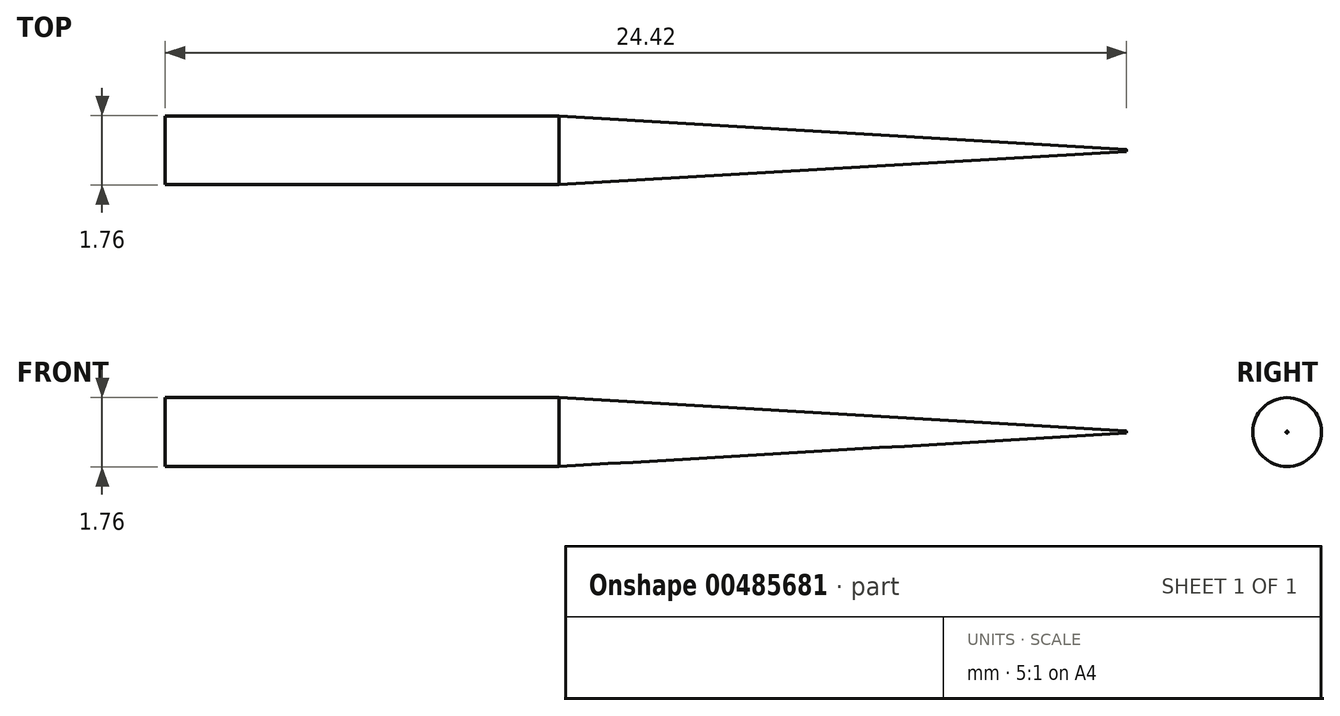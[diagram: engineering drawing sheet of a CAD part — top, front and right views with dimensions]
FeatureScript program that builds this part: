
annotation { "Feature Type Name" : "Feature", "Feature Type Description" : "" }
export const myFeature = defineFeature(function(context is Context, id is Id, definition is map)
    precondition{}
    {
        {
            var Q0;
            Q0=qCreatedBy(makeId("Front.planeOp"),FACE);
            var sketch = newSketch(context, id + "F0", { "sketchPlane" : qUnion([Q0])});
            skLineSegment(sketch, "E0", {"start": v(-10, 0.88) * mm, "end": v(0, 0.88) * mm});
            skLineSegment(sketch, "E1", {"start": v(-10, 0.88) * mm, "end": v(-10, 0) * mm});
            skLineSegment(sketch, "E2", {"start": v(14.42, 0) * mm, "end": v(-10, 0) * mm});
            skLineSegment(sketch, "E3", {"start": v(14.42, 0) * mm, "end": v(14.42, 0.03) * mm});
            skLineSegment(sketch, "E4", {"start": v(14.42, 0.02) * mm, "end": v(0, 0.88) * mm});
            skSolve(sketch);
        }
        {
            var Q0;
            Q0=makeQuery(id+"F0.imprint","IMPRINT",FACE,{"disambiguationData":[TD([[makeQuery(id+"F0.imprint","IMPRINT",EDGE,{"derivedFrom":sQuery(id+"F0.wireOp",EDGE,"E0")}),-1.0]])]});
            var Q1;
            Q1=sQuery(id+"F0.wireOp",EDGE,"E2");
            revolve(context, id + "F1", {"entities" : qUnion([Q0]), "axis" : qUnion([Q1]), "revolveType" : RevolveType.FULL});
        }
    });
